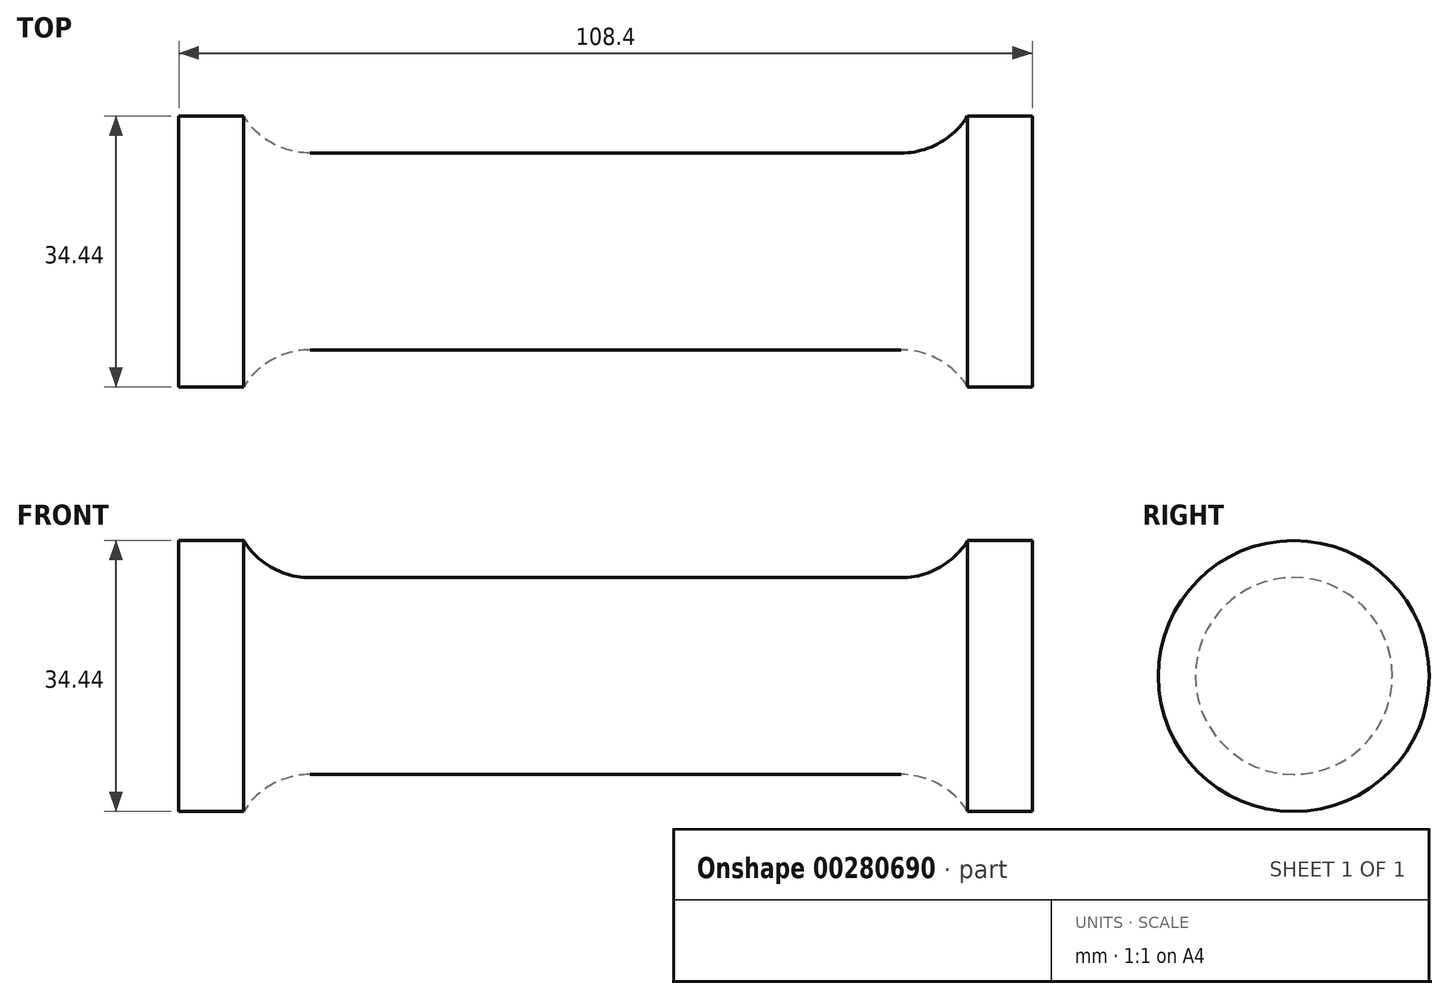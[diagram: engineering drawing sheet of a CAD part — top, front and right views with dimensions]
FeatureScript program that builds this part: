
annotation { "Feature Type Name" : "Feature", "Feature Type Description" : "" }
export const myFeature = defineFeature(function(context is Context, id is Id, definition is map)
    precondition{}
    {
        {
            var Q0;
            Q0=qCreatedBy(makeId("Front.planeOp"),FACE);
            var sketch = newSketch(context, id + "F0", { "sketchPlane" : qUnion([Q0])});
            skLineSegment(sketch, "E0", {"start": v(0, 12.5) * mm, "end": v(37.5, 12.5) * mm});
            skArc(sketch, "E1", {"start": v(37.5, 12.5) * mm, "mid": v(42.36, 13.76) * mm, "end": v(46, 17.22) * mm});
            skLineSegment(sketch, "E2", {"start": v(46, 17.22) * mm, "end": v(54.2, 17.22) * mm});
            skLineSegment(sketch, "E3", {"start": v(54.2, 17.22) * mm, "end": v(54.2, 0) * mm});
            skLineSegment(sketch, "E4.MirrorCS", {"start": v(0, 12.5) * mm, "end": v(-37.5, 12.5) * mm});
            skLineSegment(sketch, "E5.MirrorCS", {"start": v(-54.2, 17.22) * mm, "end": v(-54.2, 0) * mm});
            skLineSegment(sketch, "E6.MirrorCS", {"start": v(-46, 17.22) * mm, "end": v(-54.2, 17.22) * mm});
            skArc(sketch, "E7.MirrorCS", {"start": v(-37.5, 12.5) * mm, "mid": v(-42.36, 13.76) * mm, "end": v(-46, 17.22) * mm});
            skLineSegment(sketch, "E8", {"start": v(-54.2, 0) * mm, "end": v(54.2, 0) * mm});
            skSolve(sketch);
        }
        {
            var Q0;
            Q0=makeQuery(id+"F0.imprint","IMPRINT",FACE,{"disambiguationData":[TD([[makeQuery(id+"F0.imprint","IMPRINT",EDGE,{"derivedFrom":sQuery(id+"F0.wireOp",EDGE,"E0")}),-1.0]])]});
            var Q1;
            Q1=sQuery(id+"F0.wireOp",EDGE,"E8");
            revolve(context, id + "F1", {"entities" : qUnion([Q0]), "axis" : qUnion([Q1]), "revolveType" : RevolveType.FULL});
        }
    });
